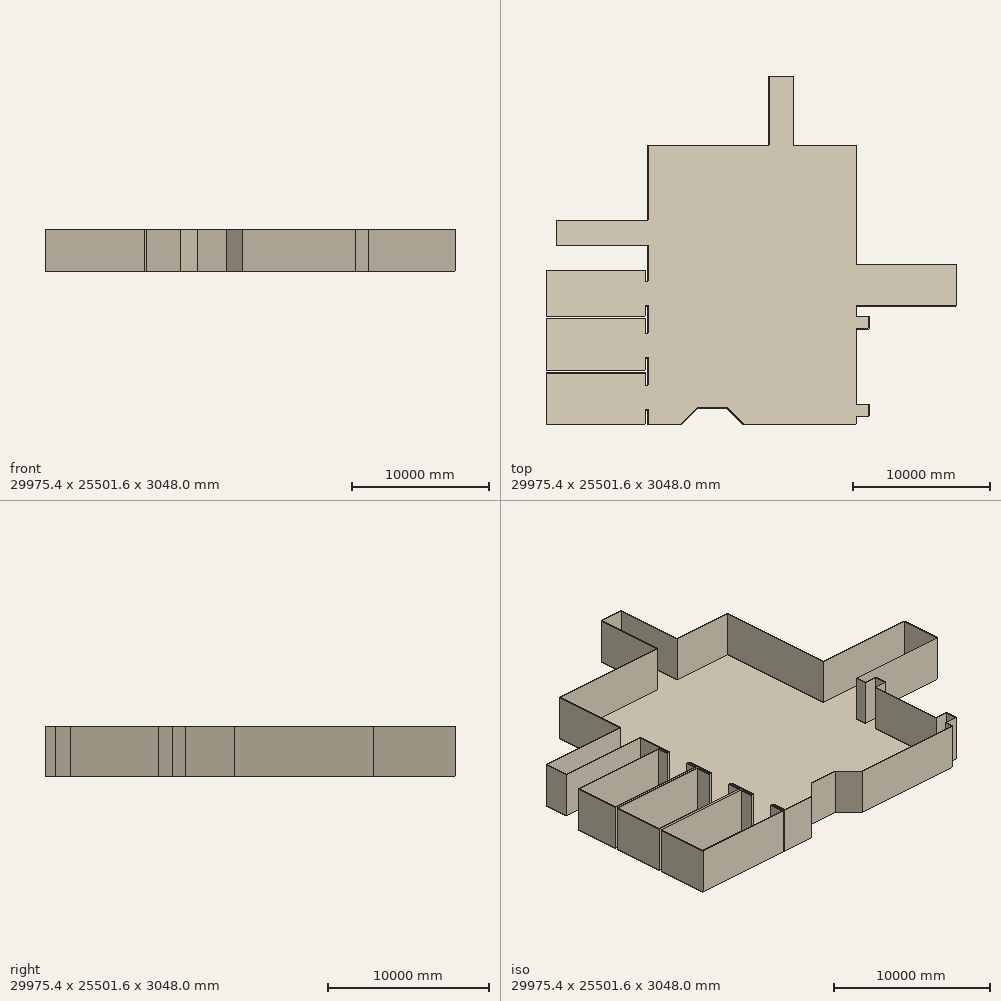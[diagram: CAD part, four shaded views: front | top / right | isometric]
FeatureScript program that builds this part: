
annotation { "Feature Type Name" : "Feature", "Feature Type Description" : "" }
export const myFeature = defineFeature(function(context is Context, id is Id, definition is map)
    precondition{}
    {
        {
            var Q0;
            Q0=qCreatedBy(makeId("Top.planeOp"),FACE);
            var sketch = newSketch(context, id + "F0", { "sketchPlane" : qUnion([Q0])});
            skLineSegment(sketch, "E0.bottom", {"start": v(-7620, 10210.8) * mm, "end": v(7620, 10210.8) * mm});
            skLineSegment(sketch, "E0.top", {"start": v(-7620, -10210.8) * mm, "end": v(7620, -10210.8) * mm});
            skLineSegment(sketch, "E0.left", {"start": v(-7620, 10210.8) * mm, "end": v(-7620, -10210.8) * mm});
            skLineSegment(sketch, "E0.right", {"start": v(7620, 10210.8) * mm, "end": v(7620, 1524) * mm});
            skLineSegment(sketch, "E1.bottom", {"start": v(7620, 1524) * mm, "end": v(14935.2, 1524) * mm});
            skLineSegment(sketch, "E1.top", {"start": v(7620, -1524) * mm, "end": v(14935.2, -1524) * mm});
            skLineSegment(sketch, "E1.right", {"start": v(14935.2, 1524) * mm, "end": v(14935.2, -1524) * mm});
            skLineSegment(sketch, "E2.trimOffspring", {"start": v(7620, -1524) * mm, "end": v(7620, -10210.8) * mm});
            skLineSegment(sketch, "E3", {"start": v(-7620, 4724.4) * mm, "end": v(-14305.29, 4724.4) * mm});
            skLineSegment(sketch, "E4", {"start": v(-14305.29, 4724.4) * mm, "end": v(-14305.29, 2895.6) * mm});
            skLineSegment(sketch, "E5", {"start": v(-14305.29, 2895.6) * mm, "end": v(-7620, 2895.6) * mm});
            skLineSegment(sketch, "E6", {"start": v(3048, 10210.8) * mm, "end": v(3048, 15290.8) * mm});
            skLineSegment(sketch, "E7", {"start": v(3048, 15290.8) * mm, "end": v(1219.2, 15290.8) * mm});
            skLineSegment(sketch, "E8", {"start": v(1219.2, 15290.8) * mm, "end": v(1219.2, 10210.8) * mm});
            skLineSegment(sketch, "E9", {"start": v(-7620, 304.8) * mm, "end": v(-7772.4, 304.8) * mm});
            skLineSegment(sketch, "E10", {"start": v(-7772.4, 304.8) * mm, "end": v(-7772.4, 1066.8) * mm});
            skLineSegment(sketch, "E11", {"start": v(-7772.4, 1066.8) * mm, "end": v(-15040.16, 1066.8) * mm});
            skLineSegment(sketch, "E12", {"start": v(-15040.16, 1066.8) * mm, "end": v(-15040.16, -2286) * mm});
            skLineSegment(sketch, "E13", {"start": v(-15040.16, -2286) * mm, "end": v(-7772.4, -2286) * mm});
            skLineSegment(sketch, "E14", {"start": v(-7772.4, -2286) * mm, "end": v(-7772.4, -1524) * mm});
            skLineSegment(sketch, "E15", {"start": v(-7772.4, -1524) * mm, "end": v(-7620, -1524) * mm});
            skLineSegment(sketch, "E16", {"start": v(-7620, -3505.2) * mm, "end": v(-7772.4, -3505.2) * mm});
            skLineSegment(sketch, "E17", {"start": v(-7772.4, -3505.2) * mm, "end": v(-7772.4, -2286) * mm});
            skLineSegment(sketch, "E18", {"start": v(-15040.16, -2286) * mm, "end": v(-15040.16, -6248.4) * mm});
            skLineSegment(sketch, "E19", {"start": v(-15040.16, -6248.4) * mm, "end": v(-7772.4, -6248.4) * mm});
            skLineSegment(sketch, "E20", {"start": v(-7772.4, -6248.4) * mm, "end": v(-7772.4, -5334) * mm});
            skLineSegment(sketch, "E21", {"start": v(-7772.4, -5334) * mm, "end": v(-7620, -5334) * mm});
            skLineSegment(sketch, "E22", {"start": v(-7620, -7315.2) * mm, "end": v(-7772.4, -7315.2) * mm});
            skLineSegment(sketch, "E23", {"start": v(-7772.4, -7315.2) * mm, "end": v(-7772.4, -6248.4) * mm});
            skLineSegment(sketch, "E24", {"start": v(-15040.16, -6248.4) * mm, "end": v(-15040.16, -10210.8) * mm});
            skLineSegment(sketch, "E25", {"start": v(-15040.16, -10210.8) * mm, "end": v(-7772.4, -10210.8) * mm});
            skLineSegment(sketch, "E26", {"start": v(-7772.4, -10210.8) * mm, "end": v(-7772.4, -9144) * mm});
            skLineSegment(sketch, "E27", {"start": v(-7772.4, -9144) * mm, "end": v(-7620, -9144) * mm});
            skLineSegment(sketch, "E28", {"start": v(-15040.16, -2438.4) * mm, "end": v(-7772.4, -2438.4) * mm});
            skLineSegment(sketch, "E29", {"start": v(-15040.16, -6400.8) * mm, "end": v(-7772.4, -6400.8) * mm});
            skPoint(sketch, "E29.startSnap0", {"position": v(-7772.4, -6400.8) * mm});
            skLineSegment(sketch, "E30", {"start": v(-15040.16, 914.4) * mm, "end": v(-7772.4, 914.4) * mm});
            skLineSegment(sketch, "E31", {"start": v(-5181.6, -10210.8) * mm, "end": v(-3962.4, -8991.6) * mm});
            skLineSegment(sketch, "E32", {"start": v(-3962.4, -8991.6) * mm, "end": v(-1828.8, -8991.6) * mm});
            skLineSegment(sketch, "E33", {"start": v(-1828.8, -8991.6) * mm, "end": v(-609.6, -10210.8) * mm});
            skLineSegment(sketch, "E34", {"start": v(7620, -9601.2) * mm, "end": v(8550.47, -9601.2) * mm});
            skLineSegment(sketch, "E35", {"start": v(8550.47, -9601.2) * mm, "end": v(8550.47, -8686.8) * mm});
            skLineSegment(sketch, "E36", {"start": v(8550.47, -8686.8) * mm, "end": v(7620, -8686.8) * mm});
            skLineSegment(sketch, "E37", {"start": v(7620, -3200.4) * mm, "end": v(8550.47, -3200.4) * mm});
            skLineSegment(sketch, "E38", {"start": v(8550.47, -3200.4) * mm, "end": v(8550.47, -2286) * mm});
            skLineSegment(sketch, "E39", {"start": v(8550.47, -2286) * mm, "end": v(7620, -2286) * mm});
            skSolve(sketch);
        }
        {
            var Q0;
            {var subQ0=sQuery(id+"F0.wireOp",EDGE,"E6");Q0=makeQuery(id+"F0.imprint","IMPRINT",FACE,{"disambiguationData":[TD([[makeQuery(id+"F0.imprint","IMPRINT",EDGE,{"derivedFrom":subQ0}),1.0]])]});}
            var Q1;
            {var subQ0=sQuery(id+"F0.wireOp",EDGE,"E3");Q1=makeQuery(id+"F0.imprint","IMPRINT",FACE,{"disambiguationData":[TD([[makeQuery(id+"F0.imprint","IMPRINT",EDGE,{"derivedFrom":subQ0}),1.0]])]});}
            var Q2;
            {var subQ0=sQuery(id+"F0.wireOp",EDGE,"E11");Q2=makeQuery(id+"F0.imprint","IMPRINT",FACE,{"disambiguationData":[TD([[makeQuery(id+"F0.imprint","IMPRINT",EDGE,{"derivedFrom":subQ0}),1.0]])]});}
            var Q3;
            {var subQ4=sQuery(id+"F0.wireOp",EDGE,"E22");Q3=makeQuery(id+"F0.imprint","IMPRINT",FACE,{"disambiguationData":[TD([[makeQuery(id+"F0.imprint","IMPRINT",EDGE,{"derivedFrom":subQ4}),1.0]])]});}
            var Q4;
            {var subQ1=sQuery(id+"F0.wireOp",EDGE,"E9");Q4=makeQuery(id+"F0.imprint","IMPRINT",FACE,{"disambiguationData":[TD([[makeQuery(id+"F0.imprint","IMPRINT",EDGE,{"derivedFrom":subQ1}),1.0]])]});}
            var Q5;
            {var subQ3=sQuery(id+"F0.wireOp",EDGE,"E16");Q5=makeQuery(id+"F0.imprint","IMPRINT",FACE,{"disambiguationData":[TD([[makeQuery(id+"F0.imprint","IMPRINT",EDGE,{"derivedFrom":subQ3}),1.0]])]});}
            var Q6;
            {var subQ12=sQuery(id+"F0.wireOp",EDGE,"E0.top");Q6=makeQuery(id+"F0.imprint","IMPRINT",FACE,{"disambiguationData":[TD([[makeQuery(id+"F0.imprint","IMPRINT",EDGE,{"derivedFrom":subQ12}),1.0]])]});}
            var Q7;
            {var subQ0=sQuery(id+"F0.wireOp",EDGE,"E34");Q7=makeQuery(id+"F0.imprint","IMPRINT",FACE,{"disambiguationData":[TD([[makeQuery(id+"F0.imprint","IMPRINT",EDGE,{"derivedFrom":subQ0}),1.0]])]});}
            var Q8;
            {var subQ0=sQuery(id+"F0.wireOp",EDGE,"E37");Q8=makeQuery(id+"F0.imprint","IMPRINT",FACE,{"disambiguationData":[TD([[makeQuery(id+"F0.imprint","IMPRINT",EDGE,{"derivedFrom":subQ0}),1.0]])]});}
            extrude(context, id + "F1", {"entities" : qUnion([Q0, Q1, Q2, Q3, Q4, Q5, Q6, Q7, Q8]), "depth" : 3048 * mm});
        }
        {
            var Q0;
            Q0=makeQuery(id+"F1.opExtrude","CAP_FACE",FACE,{"disambiguationData":[OSD([sQuery(id+"F0.wireOp",EDGE,"E0.bottom"),sQuery(id+"F0.wireOp",EDGE,"E0.top"),sQuery(id+"F0.wireOp",EDGE,"E0.left"),sQuery(id+"F0.wireOp",EDGE,"E0.right"),sQuery(id+"F0.wireOp",EDGE,"E1.bottom"),sQuery(id+"F0.wireOp",EDGE,"E1.top"),sQuery(id+"F0.wireOp",EDGE,"E1.right"),sQuery(id+"F0.wireOp",EDGE,"E2.trimOffspring")])],"isStart":false});
            shell(context, id + "F2", {"entities" : qUnion([Q0]), "thickness" : 25.4 * mm});
        }
    });
